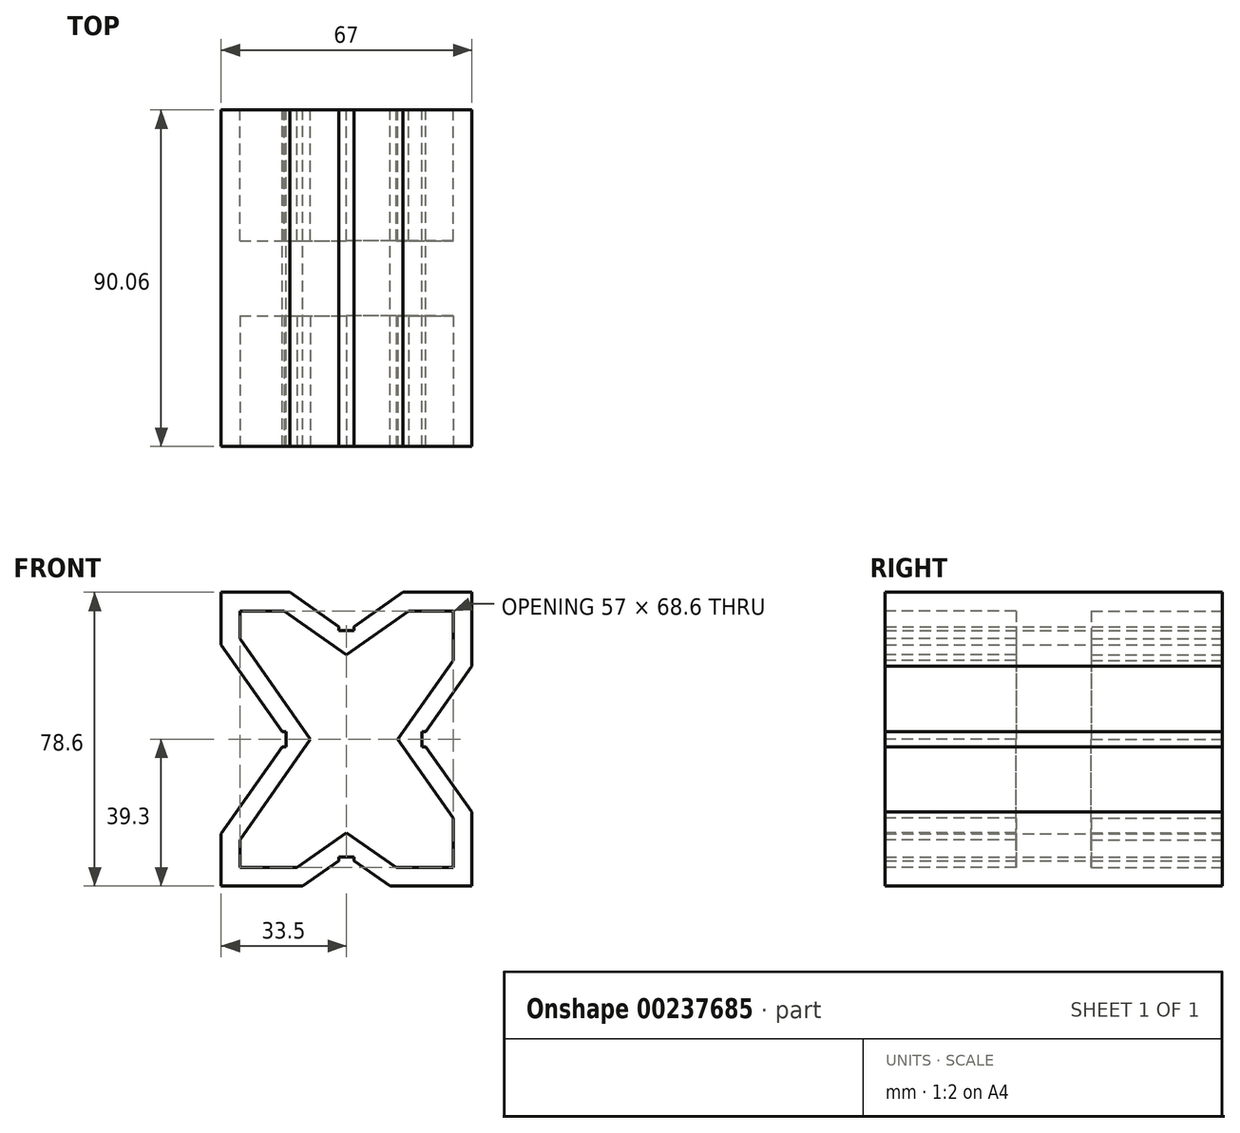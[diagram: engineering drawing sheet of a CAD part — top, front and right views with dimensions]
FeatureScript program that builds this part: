
annotation { "Feature Type Name" : "Feature", "Feature Type Description" : "" }
export const myFeature = defineFeature(function(context is Context, id is Id, definition is map)
    precondition{}
    {
        {
            var Q0;
            Q0=qCreatedBy(makeId("Front.planeOp"),FACE);
            var sketch = newSketch(context, id + "F0", { "sketchPlane" : qUnion([Q0])});
            skLineSegment(sketch, "E0", {"start": v(0, 0) * mm, "end": v(67, 0) * mm});
            skPoint(sketch, "E1", {"position": v(18.4, 0) * mm});
            skPoint(sketch, "E2", {"position": v(48.6, 0) * mm});
            skLineSegment(sketch, "E3", {"start": v(0, 0) * mm, "end": v(0, -78.6) * mm});
            skLineSegment(sketch, "E4", {"start": v(67, 0) * mm, "end": v(67, -78.6) * mm});
            skLineSegment(sketch, "E5", {"start": v(0, -78.6) * mm, "end": v(67, -78.6) * mm});
            skPoint(sketch, "E6", {"position": v(0, -14) * mm});
            skPoint(sketch, "E7", {"position": v(0, -64.6) * mm});
            skPoint(sketch, "E8.endSnap0", {"position": v(0, -39.3) * mm});
            skLineSegment(sketch, "E9", {"start": v(0, -64.6) * mm, "end": v(16.31, -41.3) * mm});
            skLineSegment(sketch, "E10", {"start": v(0, -14) * mm, "end": v(16.31, -37.3) * mm});
            skPoint(sketch, "E11.orphan", {"position": v(24.15, -39.3) * mm});
            skPoint(sketch, "E12", {"position": v(16.31, -37.3) * mm});
            skPoint(sketch, "E13", {"position": v(16.31, -41.3) * mm});
            skLineSegment(sketch, "E14", {"start": v(16.31, -37.3) * mm, "end": v(17.34, -37.3) * mm});
            skLineSegment(sketch, "E15", {"start": v(16.31, -41.3) * mm, "end": v(17.34, -41.3) * mm});
            skLineSegment(sketch, "E16", {"start": v(17.34, -37.3) * mm, "end": v(17.34, -41.3) * mm});
            skPoint(sketch, "E17", {"position": v(67, -19.8) * mm});
            skPoint(sketch, "E18", {"position": v(67, -58.8) * mm});
            skLineSegment(sketch, "E19", {"start": v(67, -58.8) * mm, "end": v(54.75, -41.3) * mm});
            skLineSegment(sketch, "E20", {"start": v(67, -19.8) * mm, "end": v(54.75, -37.3) * mm});
            skPoint(sketch, "E21.start.orphan", {"position": v(67, -39.3) * mm});
            skPoint(sketch, "E22", {"position": v(54.75, -37.3) * mm});
            skPoint(sketch, "E23", {"position": v(54.75, -41.3) * mm});
            skLineSegment(sketch, "E24", {"start": v(54.75, -37.3) * mm, "end": v(53.72, -37.3) * mm});
            skLineSegment(sketch, "E25", {"start": v(54.75, -41.3) * mm, "end": v(53.72, -41.3) * mm});
            skLineSegment(sketch, "E26", {"start": v(53.72, -41.3) * mm, "end": v(53.72, -37.3) * mm});
            skPoint(sketch, "E27", {"position": v(21.8, -78.6) * mm});
            skPoint(sketch, "E28", {"position": v(45.2, -78.6) * mm});
            skLineSegment(sketch, "E29", {"start": v(21.8, -78.6) * mm, "end": v(31.5, -71.8) * mm});
            skLineSegment(sketch, "E30", {"start": v(45.2, -78.6) * mm, "end": v(35.5, -71.8) * mm});
            skPoint(sketch, "E31", {"position": v(31.5, -71.8) * mm});
            skPoint(sketch, "E32", {"position": v(35.5, -71.8) * mm});
            skLineSegment(sketch, "E33", {"start": v(35.5, -71.8) * mm, "end": v(35.5, -70.78) * mm});
            skLineSegment(sketch, "E34", {"start": v(31.5, -71.8) * mm, "end": v(31.5, -70.78) * mm});
            skLineSegment(sketch, "E35", {"start": v(31.5, -70.78) * mm, "end": v(35.5, -70.78) * mm});
            skLineSegment(sketch, "E36", {"start": v(18.4, 0) * mm, "end": v(31.5, -9.17) * mm});
            skLineSegment(sketch, "E37", {"start": v(48.6, 0) * mm, "end": v(35.5, -9.17) * mm});
            skPoint(sketch, "E38", {"position": v(31.5, -9.17) * mm});
            skPoint(sketch, "E39", {"position": v(35.5, -9.17) * mm});
            skLineSegment(sketch, "E40", {"start": v(31.5, -9.17) * mm, "end": v(31.5, -10.2) * mm});
            skLineSegment(sketch, "E41", {"start": v(35.5, -9.17) * mm, "end": v(35.5, -10.2) * mm});
            skLineSegment(sketch, "E42", {"start": v(31.5, -10.2) * mm, "end": v(35.5, -10.2) * mm});
            skLineSegment(sketch, "E43.trimOffspring", {"start": v(17.34, -38.76) * mm, "end": v(17.72, -39.3) * mm});
            skLineSegment(sketch, "E44.trimOffspring", {"start": v(17.34, -39.84) * mm, "end": v(17.72, -39.3) * mm});
            skLineSegment(sketch, "E45.trimOffspring", {"start": v(53.72, -38.76) * mm, "end": v(53.35, -39.3) * mm});
            skLineSegment(sketch, "E46.trimOffspring", {"start": v(53.72, -39.84) * mm, "end": v(53.35, -39.3) * mm});
            skLineSegment(sketch, "E47.trimOffspring", {"start": v(34.04, -70.78) * mm, "end": v(33.5, -70.4) * mm});
            skLineSegment(sketch, "E48.trimOffspring", {"start": v(32.96, -70.78) * mm, "end": v(33.5, -70.4) * mm});
            skLineSegment(sketch, "E49.trimOffspring", {"start": v(34.04, -10.2) * mm, "end": v(33.5, -10.57) * mm});
            skLineSegment(sketch, "E50.trimOffspring", {"start": v(32.96, -10.2) * mm, "end": v(33.5, -10.57) * mm});
            skSolve(sketch);
        }
        {
            var Q0;
            {var subQ13=sQuery(id+"F0.wireOp",EDGE,"E9");Q0=makeQuery(id+"F0.imprint","IMPRINT",FACE,{"disambiguationData":[TD([[makeQuery(id+"F0.imprint","IMPRINT",EDGE,{"derivedFrom":subQ13}),-1.0]])]});}
            var Q1;
            {var subQ0=sQuery(id+"F0.wireOp",EDGE,"E45.trimOffspring");Q1=makeQuery(id+"F0.imprint","IMPRINT",FACE,{"disambiguationData":[TD([[makeQuery(id+"F0.imprint","IMPRINT",EDGE,{"derivedFrom":subQ0}),1.0]])]});}
            var Q2;
            {var subQ0=sQuery(id+"F0.wireOp",EDGE,"E43.trimOffspring");Q2=makeQuery(id+"F0.imprint","IMPRINT",FACE,{"disambiguationData":[TD([[makeQuery(id+"F0.imprint","IMPRINT",EDGE,{"derivedFrom":subQ0}),-1.0]])]});}
            var Q3;
            {var subQ0=sQuery(id+"F0.wireOp",EDGE,"E49.trimOffspring");Q3=makeQuery(id+"F0.imprint","IMPRINT",FACE,{"disambiguationData":[TD([[makeQuery(id+"F0.imprint","IMPRINT",EDGE,{"derivedFrom":subQ0}),-1.0]])]});}
            var Q4;
            {var subQ0=sQuery(id+"F0.wireOp",EDGE,"E47.trimOffspring");Q4=makeQuery(id+"F0.imprint","IMPRINT",FACE,{"disambiguationData":[TD([[makeQuery(id+"F0.imprint","IMPRINT",EDGE,{"derivedFrom":subQ0}),1.0]])]});}
            extrude(context, id + "F1", {"entities" : qUnion([Q0, Q1, Q2, Q3, Q4]), "depth" : 45.02 * mm});
        }
        {
            var Q0;
            Q0=makeQuery(id+"F1.opExtrude","CAP_FACE",FACE,{"disambiguationData":[OSD([sQuery(id+"F0.wireOp",EDGE,"E0"),sQuery(id+"F0.wireOp",EDGE,"E3"),sQuery(id+"F0.wireOp",EDGE,"E4"),sQuery(id+"F0.wireOp",EDGE,"E5"),sQuery(id+"F0.wireOp",EDGE,"E9"),sQuery(id+"F0.wireOp",EDGE,"E10"),sQuery(id+"F0.wireOp",EDGE,"E14"),sQuery(id+"F0.wireOp",EDGE,"E15"),sQuery(id+"F0.wireOp",EDGE,"E16"),sQuery(id+"F0.wireOp",EDGE,"E19"),sQuery(id+"F0.wireOp",EDGE,"E20"),sQuery(id+"F0.wireOp",EDGE,"E24"),sQuery(id+"F0.wireOp",EDGE,"E25"),sQuery(id+"F0.wireOp",EDGE,"E26"),sQuery(id+"F0.wireOp",EDGE,"E29"),sQuery(id+"F0.wireOp",EDGE,"E30"),sQuery(id+"F0.wireOp",EDGE,"E33"),sQuery(id+"F0.wireOp",EDGE,"E34"),sQuery(id+"F0.wireOp",EDGE,"E35"),sQuery(id+"F0.wireOp",EDGE,"E36"),sQuery(id+"F0.wireOp",EDGE,"E37"),sQuery(id+"F0.wireOp",EDGE,"E40"),sQuery(id+"F0.wireOp",EDGE,"E41"),sQuery(id+"F0.wireOp",EDGE,"E42")])],"isStart":false});
            var sketch = newSketch(context, id + "F2", { "sketchPlane" : qUnion([Q0])});
            skLineSegment(sketch, "E51.0", {"start": v(16.82, -5) * mm, "end": v(28.63, -13.27) * mm});
            skLineSegment(sketch, "E51.1", {"start": v(5, -5) * mm, "end": v(16.82, -5) * mm});
            skLineSegment(sketch, "E51.2", {"start": v(5, -5) * mm, "end": v(5, -12.42) * mm});
            skLineSegment(sketch, "E51.3", {"start": v(5, -12.42) * mm, "end": v(20.41, -34.43) * mm});
            skLineSegment(sketch, "E52.0", {"start": v(20.22, -73.6) * mm, "end": v(28.63, -67.71) * mm});
            skLineSegment(sketch, "E52.1", {"start": v(5, -73.6) * mm, "end": v(20.22, -73.6) * mm});
            skLineSegment(sketch, "E52.2", {"start": v(5, -66.18) * mm, "end": v(5, -73.6) * mm});
            skLineSegment(sketch, "E52.3", {"start": v(5, -66.18) * mm, "end": v(20.41, -44.17) * mm});
            skLineSegment(sketch, "E53.0", {"start": v(46.78, -73.6) * mm, "end": v(38.37, -67.71) * mm});
            skLineSegment(sketch, "E53.1", {"start": v(46.78, -73.6) * mm, "end": v(62, -73.6) * mm});
            skLineSegment(sketch, "E53.2", {"start": v(62, -60.38) * mm, "end": v(62, -73.6) * mm});
            skLineSegment(sketch, "E53.3", {"start": v(62, -60.38) * mm, "end": v(50.65, -44.17) * mm});
            skLineSegment(sketch, "E54.0", {"start": v(62, -18.22) * mm, "end": v(50.65, -34.43) * mm});
            skLineSegment(sketch, "E54.1", {"start": v(62, -5) * mm, "end": v(62, -18.22) * mm});
            skLineSegment(sketch, "E54.2", {"start": v(50.18, -5) * mm, "end": v(62, -5) * mm});
            skLineSegment(sketch, "E54.3", {"start": v(50.18, -5) * mm, "end": v(38.37, -13.27) * mm});
            skLineSegment(sketch, "E55", {"start": v(20.41, -44.17) * mm, "end": v(23.82, -39.3) * mm});
            skLineSegment(sketch, "E56", {"start": v(20.41, -34.43) * mm, "end": v(23.82, -39.3) * mm});
            skLineSegment(sketch, "E57", {"start": v(38.37, -13.27) * mm, "end": v(33.5, -16.68) * mm});
            skLineSegment(sketch, "E58", {"start": v(28.63, -13.27) * mm, "end": v(33.5, -16.68) * mm});
            skLineSegment(sketch, "E59", {"start": v(50.65, -44.17) * mm, "end": v(47.24, -39.3) * mm});
            skLineSegment(sketch, "E60", {"start": v(50.65, -34.43) * mm, "end": v(47.24, -39.3) * mm});
            skLineSegment(sketch, "E61", {"start": v(28.63, -67.71) * mm, "end": v(33.5, -64.3) * mm});
            skLineSegment(sketch, "E62", {"start": v(38.37, -67.71) * mm, "end": v(33.5, -64.3) * mm});
            skSolve(sketch);
        }
        {
            var Q0;
            Q0=makeQuery(id+"F2.imprint","IMPRINT",FACE,{"disambiguationData":[TD([[makeQuery(id+"F2.imprint","IMPRINT",EDGE,{"derivedFrom":sQuery(id+"F2.wireOp",EDGE,"E51.0")}),-1.0]])]});
            extrude(context, id + "F3", {"entities" : qUnion([Q0]), "operationType" : NewBodyOperationType.REMOVE, "oppositeDirection" : true, "depth" : 35 * mm});
        }
        {
            var Q0;
            Q0=makeQuery(id+"F1.opExtrude","SWEPT_BODY",BODY,{"disambiguationData":[OSD([sQuery(id+"F0.wireOp",EDGE,"E0"),sQuery(id+"F0.wireOp",EDGE,"E3"),sQuery(id+"F0.wireOp",EDGE,"E4"),sQuery(id+"F0.wireOp",EDGE,"E5"),sQuery(id+"F0.wireOp",EDGE,"E9"),sQuery(id+"F0.wireOp",EDGE,"E10"),sQuery(id+"F0.wireOp",EDGE,"E14"),sQuery(id+"F0.wireOp",EDGE,"E15"),sQuery(id+"F0.wireOp",EDGE,"E16"),sQuery(id+"F0.wireOp",EDGE,"E19"),sQuery(id+"F0.wireOp",EDGE,"E20"),sQuery(id+"F0.wireOp",EDGE,"E24"),sQuery(id+"F0.wireOp",EDGE,"E25"),sQuery(id+"F0.wireOp",EDGE,"E26"),sQuery(id+"F0.wireOp",EDGE,"E29"),sQuery(id+"F0.wireOp",EDGE,"E30"),sQuery(id+"F0.wireOp",EDGE,"E33"),sQuery(id+"F0.wireOp",EDGE,"E34"),sQuery(id+"F0.wireOp",EDGE,"E35"),sQuery(id+"F0.wireOp",EDGE,"E36"),sQuery(id+"F0.wireOp",EDGE,"E37"),sQuery(id+"F0.wireOp",EDGE,"E40"),sQuery(id+"F0.wireOp",EDGE,"E41"),sQuery(id+"F0.wireOp",EDGE,"E42")])]});
            var Q1;
            Q1=makeQuery(id+"F1.opExtrude","CAP_FACE",FACE,{"disambiguationData":[OSD([sQuery(id+"F0.wireOp",EDGE,"E0"),sQuery(id+"F0.wireOp",EDGE,"E3"),sQuery(id+"F0.wireOp",EDGE,"E4"),sQuery(id+"F0.wireOp",EDGE,"E5"),sQuery(id+"F0.wireOp",EDGE,"E9"),sQuery(id+"F0.wireOp",EDGE,"E10"),sQuery(id+"F0.wireOp",EDGE,"E14"),sQuery(id+"F0.wireOp",EDGE,"E15"),sQuery(id+"F0.wireOp",EDGE,"E16"),sQuery(id+"F0.wireOp",EDGE,"E19"),sQuery(id+"F0.wireOp",EDGE,"E20"),sQuery(id+"F0.wireOp",EDGE,"E24"),sQuery(id+"F0.wireOp",EDGE,"E25"),sQuery(id+"F0.wireOp",EDGE,"E26"),sQuery(id+"F0.wireOp",EDGE,"E29"),sQuery(id+"F0.wireOp",EDGE,"E30"),sQuery(id+"F0.wireOp",EDGE,"E33"),sQuery(id+"F0.wireOp",EDGE,"E34"),sQuery(id+"F0.wireOp",EDGE,"E35"),sQuery(id+"F0.wireOp",EDGE,"E36"),sQuery(id+"F0.wireOp",EDGE,"E37"),sQuery(id+"F0.wireOp",EDGE,"E40"),sQuery(id+"F0.wireOp",EDGE,"E41"),sQuery(id+"F0.wireOp",EDGE,"E42")])],"isStart":true});
            mirror(context, id + "F4", {"operationType" : NewBodyOperationType.ADD, "entities" : qUnion([Q0]), "mirrorPlane" : qUnion([Q1])});
        }
    });
